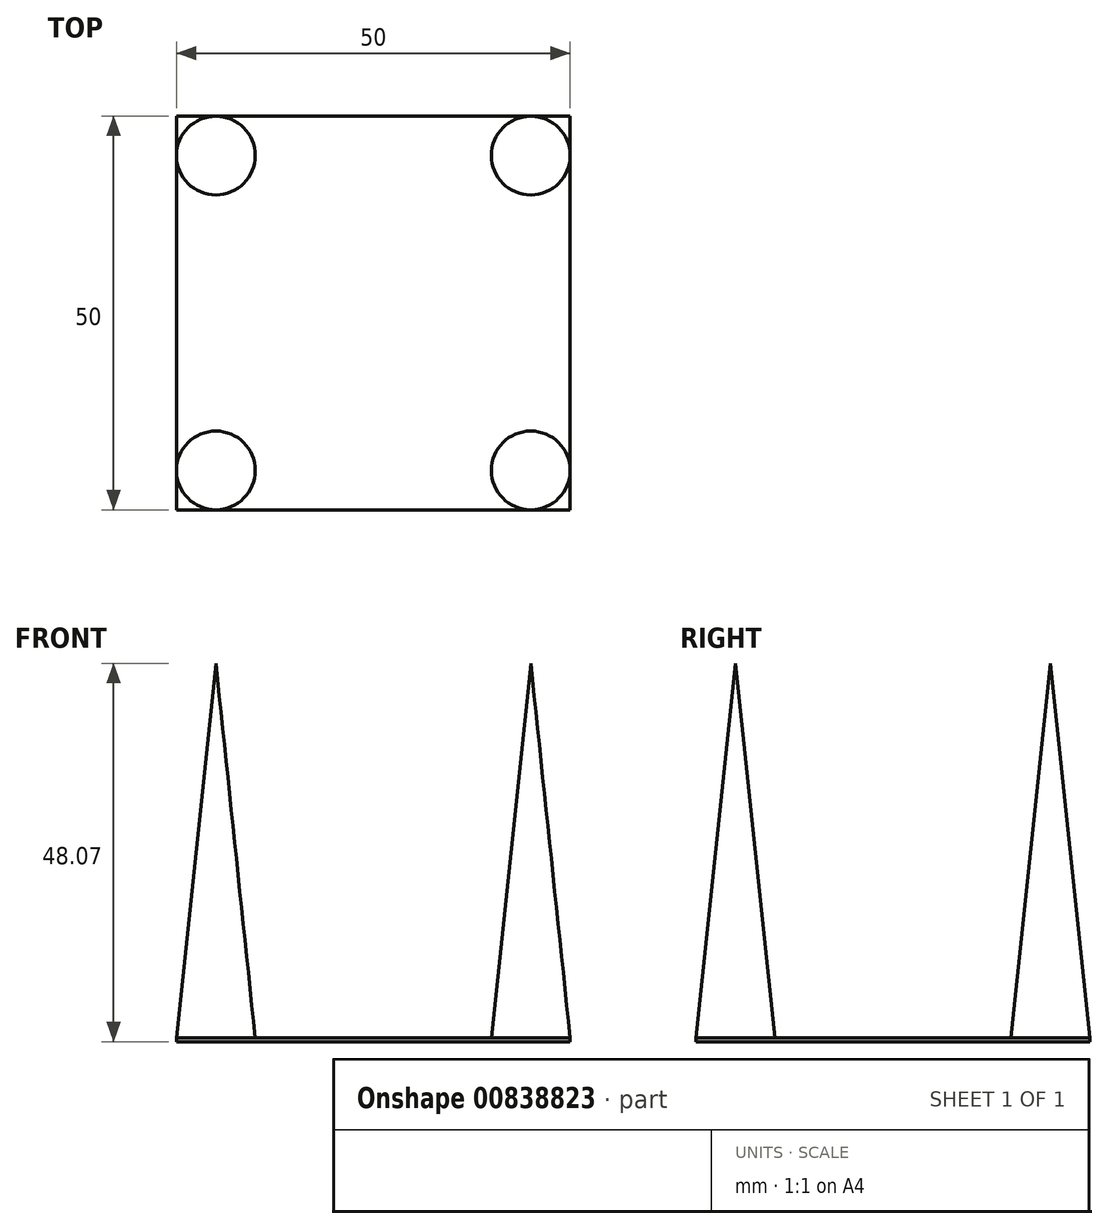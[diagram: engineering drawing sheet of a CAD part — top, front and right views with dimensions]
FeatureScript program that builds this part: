
annotation { "Feature Type Name" : "Feature", "Feature Type Description" : "" }
export const myFeature = defineFeature(function(context is Context, id is Id, definition is map)
    precondition{}
    {
        {
            var Q0;
            Q0=qCreatedBy(makeId("Top.planeOp"),FACE);
            var sketch = newSketch(context, id + "F0", { "sketchPlane" : qUnion([Q0])});
            skLineSegment(sketch, "E0.bottom", {"start": v(25, -25) * mm, "end": v(-25, -25) * mm});
            skLineSegment(sketch, "E0.top", {"start": v(25, 25) * mm, "end": v(-25, 25) * mm});
            skLineSegment(sketch, "E0.left", {"start": v(25, -25) * mm, "end": v(25, 25) * mm});
            skLineSegment(sketch, "E0.right", {"start": v(-25, -25) * mm, "end": v(-25, 25) * mm});
            skPoint(sketch, "E0.middle", {"position": v(0, 0) * mm});
            skCircle(sketch, "E1", {"center": v(-20, -20) * mm, "radius": 5 * mm});
            skCircle(sketch, "E2", {"center": v(-20, 20) * mm, "radius": 5 * mm});
            skCircle(sketch, "E3", {"center": v(20, 20) * mm, "radius": 5 * mm});
            skCircle(sketch, "E4", {"center": v(20, -20) * mm, "radius": 5 * mm});
            skSolve(sketch);
        }
        {
            var Q0;
            {var subQ5=sQuery(id+"F0.wireOp",EDGE,"E4");var subQ10=sQuery(id+"F0.wireOp",EDGE,"E0.bottom");var subQ11=makeQuery(id+"F0.imprint","INTERSECT",VERTEX,{"derivedFrom":[subQ10,subQ5]});Q0=makeQuery(id+"F0.imprint","IMPRINT",FACE,{"disambiguationData":[TD([[makeQuery(id+"F0.imprint","IMPRINT",EDGE,{"disambiguationData":[TD([[subQ11,-1.0]])],"derivedFrom":subQ10}),-1.0]])]});}
            var Q1;
            {var subQ0=sQuery(id+"F0.wireOp",EDGE,"E2");var subQ1=makeQuery(id+"F0.imprint","INTERSECT",VERTEX,{"derivedFrom":[sQuery(id+"F0.wireOp",EDGE,"E0.top"),subQ0]});Q1=makeQuery(id+"F0.imprint","IMPRINT",FACE,{"disambiguationData":[TD([[makeQuery(id+"F0.imprint","IMPRINT",EDGE,{"disambiguationData":[TD([[subQ1,-1.0]])],"derivedFrom":subQ0}),1.0]])]});}
            var Q2;
            {var subQ0=sQuery(id+"F0.wireOp",EDGE,"E0.right");var subQ1=sQuery(id+"F0.wireOp",EDGE,"E0.top");var subQ2=makeQuery(id+"F0.imprint","INTERSECT",VERTEX,{"derivedFrom":[subQ1,subQ0]});Q2=makeQuery(id+"F0.imprint","IMPRINT",FACE,{"disambiguationData":[TD([[makeQuery(id+"F0.imprint","IMPRINT",EDGE,{"disambiguationData":[TD([[subQ2,1.0]])],"derivedFrom":subQ1}),1.0]])]});}
            var Q3;
            {var subQ0=sQuery(id+"F0.wireOp",EDGE,"E3");var subQ1=makeQuery(id+"F0.imprint","INTERSECT",VERTEX,{"derivedFrom":[sQuery(id+"F0.wireOp",EDGE,"E0.top"),subQ0]});Q3=makeQuery(id+"F0.imprint","IMPRINT",FACE,{"disambiguationData":[TD([[makeQuery(id+"F0.imprint","IMPRINT",EDGE,{"disambiguationData":[TD([[subQ1,1.0]])],"derivedFrom":subQ0}),1.0]])]});}
            var Q4;
            {var subQ0=sQuery(id+"F0.wireOp",EDGE,"E0.left");var subQ1=sQuery(id+"F0.wireOp",EDGE,"E0.top");var subQ2=makeQuery(id+"F0.imprint","INTERSECT",VERTEX,{"derivedFrom":[subQ1,subQ0]});Q4=makeQuery(id+"F0.imprint","IMPRINT",FACE,{"disambiguationData":[TD([[makeQuery(id+"F0.imprint","IMPRINT",EDGE,{"disambiguationData":[TD([[subQ2,-1.0]])],"derivedFrom":subQ1}),1.0]])]});}
            var Q5;
            {var subQ0=sQuery(id+"F0.wireOp",EDGE,"E4");var subQ1=makeQuery(id+"F0.imprint","INTERSECT",VERTEX,{"derivedFrom":[sQuery(id+"F0.wireOp",EDGE,"E0.bottom"),subQ0]});Q5=makeQuery(id+"F0.imprint","IMPRINT",FACE,{"disambiguationData":[TD([[makeQuery(id+"F0.imprint","IMPRINT",EDGE,{"disambiguationData":[TD([[subQ1,1.0]])],"derivedFrom":subQ0}),1.0]])]});}
            var Q6;
            {var subQ0=sQuery(id+"F0.wireOp",EDGE,"E0.left");var subQ1=sQuery(id+"F0.wireOp",EDGE,"E0.bottom");var subQ2=makeQuery(id+"F0.imprint","INTERSECT",VERTEX,{"derivedFrom":[subQ1,subQ0]});Q6=makeQuery(id+"F0.imprint","IMPRINT",FACE,{"disambiguationData":[TD([[makeQuery(id+"F0.imprint","IMPRINT",EDGE,{"disambiguationData":[TD([[subQ2,-1.0]])],"derivedFrom":subQ1}),-1.0]])]});}
            var Q7;
            {var subQ0=sQuery(id+"F0.wireOp",EDGE,"E1");var subQ1=makeQuery(id+"F0.imprint","INTERSECT",VERTEX,{"derivedFrom":[sQuery(id+"F0.wireOp",EDGE,"E0.bottom"),subQ0]});Q7=makeQuery(id+"F0.imprint","IMPRINT",FACE,{"disambiguationData":[TD([[makeQuery(id+"F0.imprint","IMPRINT",EDGE,{"disambiguationData":[TD([[subQ1,1.0]])],"derivedFrom":subQ0}),1.0]])]});}
            var Q8;
            {var subQ0=sQuery(id+"F0.wireOp",EDGE,"E0.right");var subQ1=sQuery(id+"F0.wireOp",EDGE,"E0.bottom");var subQ2=makeQuery(id+"F0.imprint","INTERSECT",VERTEX,{"derivedFrom":[subQ1,subQ0]});Q8=makeQuery(id+"F0.imprint","IMPRINT",FACE,{"disambiguationData":[TD([[makeQuery(id+"F0.imprint","IMPRINT",EDGE,{"disambiguationData":[TD([[subQ2,1.0]])],"derivedFrom":subQ1}),-1.0]])]});}
            extrude(context, id + "F1", {"entities" : qUnion([Q0, Q1, Q2, Q3, Q4, Q5, Q6, Q7, Q8]), "oppositeDirection" : true, "depth" : .5 * mm, "offsetDistance" : 25 * mm});
        }
        {
            var Q0;
            {var subQ0=sQuery(id+"F0.wireOp",EDGE,"E2");var subQ1=makeQuery(id+"F0.imprint","INTERSECT",VERTEX,{"derivedFrom":[sQuery(id+"F0.wireOp",EDGE,"E0.top"),subQ0]});Q0=makeQuery(id+"F0.imprint","IMPRINT",FACE,{"disambiguationData":[TD([[makeQuery(id+"F0.imprint","IMPRINT",EDGE,{"disambiguationData":[TD([[subQ1,-1.0]])],"derivedFrom":subQ0}),1.0]])]});}
            var Q1;
            {var subQ0=sQuery(id+"F0.wireOp",EDGE,"E3");var subQ1=makeQuery(id+"F0.imprint","INTERSECT",VERTEX,{"derivedFrom":[sQuery(id+"F0.wireOp",EDGE,"E0.top"),subQ0]});Q1=makeQuery(id+"F0.imprint","IMPRINT",FACE,{"disambiguationData":[TD([[makeQuery(id+"F0.imprint","IMPRINT",EDGE,{"disambiguationData":[TD([[subQ1,1.0]])],"derivedFrom":subQ0}),1.0]])]});}
            var Q2;
            {var subQ0=sQuery(id+"F0.wireOp",EDGE,"E4");var subQ1=makeQuery(id+"F0.imprint","INTERSECT",VERTEX,{"derivedFrom":[sQuery(id+"F0.wireOp",EDGE,"E0.bottom"),subQ0]});Q2=makeQuery(id+"F0.imprint","IMPRINT",FACE,{"disambiguationData":[TD([[makeQuery(id+"F0.imprint","IMPRINT",EDGE,{"disambiguationData":[TD([[subQ1,1.0]])],"derivedFrom":subQ0}),1.0]])]});}
            var Q3;
            {var subQ0=sQuery(id+"F0.wireOp",EDGE,"E1");var subQ1=makeQuery(id+"F0.imprint","INTERSECT",VERTEX,{"derivedFrom":[sQuery(id+"F0.wireOp",EDGE,"E0.bottom"),subQ0]});Q3=makeQuery(id+"F0.imprint","IMPRINT",FACE,{"disambiguationData":[TD([[makeQuery(id+"F0.imprint","IMPRINT",EDGE,{"disambiguationData":[TD([[subQ1,1.0]])],"derivedFrom":subQ0}),1.0]])]});}
            extrude(context, id + "F2", {"entities" : qUnion([Q0, Q1, Q2, Q3]), "operationType" : NewBodyOperationType.ADD, "depth" : 50 * mm, "offsetDistance" : 25 * mm, "hasDraft" : true, "draftAngle" : 6 * degree, "draftPullDirection" : true});
        }
    });
